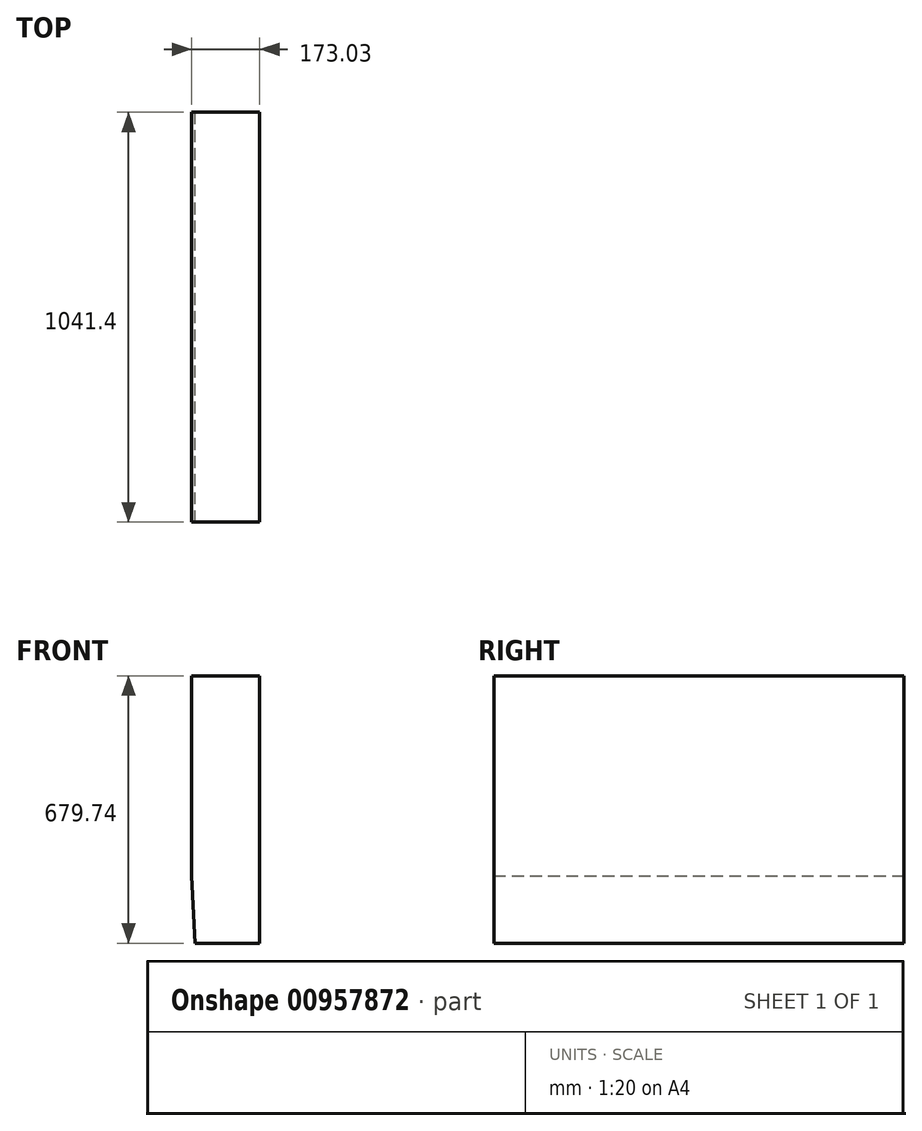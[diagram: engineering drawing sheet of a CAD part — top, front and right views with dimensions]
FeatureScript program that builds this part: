
annotation { "Feature Type Name" : "Feature", "Feature Type Description" : "" }
export const myFeature = defineFeature(function(context is Context, id is Id, definition is map)
    precondition{}
    {
        {
            var Q0;
            Q0=qCreatedBy(makeId("Front.planeOp"),FACE);
            var sketch = newSketch(context, id + "F0", { "sketchPlane" : qUnion([Q0])});
            skLineSegment(sketch, "E0", {"start": v(-86.46, 88.8) * mm, "end": v(86.57, 88.8) * mm});
            skLineSegment(sketch, "E1", {"start": v(86.57, 88.8) * mm, "end": v(86.57, -82.93) * mm});
            skLineSegment(sketch, "E2", {"start": v(86.57, -82.93) * mm, "end": v(-77.6, -82.93) * mm});
            skLineSegment(sketch, "E3", {"start": v(-77.6, -82.93) * mm, "end": v(-86.46, 88.8) * mm});
            skSolve(sketch);
        }
        {
            var Q0;
            Q0=makeQuery(id+"F0.imprint","IMPRINT",FACE,{"disambiguationData":[TD([[makeQuery(id+"F0.imprint","IMPRINT",EDGE,{"derivedFrom":sQuery(id+"F0.wireOp",EDGE,"E0")}),-1.0]])]});
            extrude(context, id + "F1", {"entities" : qUnion([Q0]), "depth" : 25.4 * mm, "offsetDistance" : 25.4 * mm});
        }
        {
            var Q0;
            Q0=makeQuery(id+"F1.opExtrude","CAP_FACE",FACE,{"disambiguationData":[OSD([sQuery(id+"F0.wireOp",EDGE,"E0"),sQuery(id+"F0.wireOp",EDGE,"E1"),sQuery(id+"F0.wireOp",EDGE,"E2"),sQuery(id+"F0.wireOp",EDGE,"E3")])],"isStart":false});
            extrude(context, id + "F2", {"entities" : qUnion([Q0]), "operationType" : NewBodyOperationType.ADD, "depth" : 508 * mm, "offsetDistance" : 25.4 * mm});
        }
        {
            var Q0;
            Q0=makeQuery(id+"F2.opExtrude","CAP_FACE",FACE,{"disambiguationData":[OSD([sQuery(id+"F0.wireOp",EDGE,"E0"),sQuery(id+"F0.wireOp",EDGE,"E1"),sQuery(id+"F0.wireOp",EDGE,"E2"),sQuery(id+"F0.wireOp",EDGE,"E3")])],"isStart":false});
            extrude(context, id + "F3", {"entities" : qUnion([Q0]), "operationType" : NewBodyOperationType.ADD, "depth" : 508 * mm, "offsetDistance" : 25.4 * mm});
        }
        {
            var Q0;
            {var subQ0=sQuery(id+"F0.wireOp",EDGE,"E0");Q0=makeQuery(id+"F3.boolean.opBoolean","MERGE",FACE,{"derivedFrom":[makeQuery(id+"F2.boolean.opBoolean","MERGE",FACE,{"derivedFrom":[makeQuery(id+"F1.opExtrude","SWEPT_FACE",FACE,{"disambiguationData":[OSD([subQ0])]}),makeQuery(id+"F2.opExtrude","SWEPT_FACE",FACE,{"disambiguationData":[OSD([subQ0])]})]}),makeQuery(id+"F3.opExtrude","SWEPT_FACE",FACE,{"disambiguationData":[OSD([subQ0])]})]});}
            extrude(context, id + "F4", {"entities" : qUnion([Q0]), "operationType" : NewBodyOperationType.ADD, "depth" : 508 * mm, "offsetDistance" : 25.4 * mm});
        }
    });
